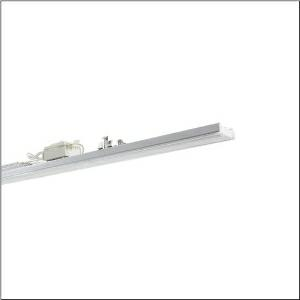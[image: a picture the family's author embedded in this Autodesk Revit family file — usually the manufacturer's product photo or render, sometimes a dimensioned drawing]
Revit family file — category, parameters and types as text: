
# Revit family: licross_r__21_recessed_ho_52tl12cn495m_a1ad
name_source: partatom
category: Lighting Fixtures
units: mm (PartAtom-declared; Revit-internal decimal feet)

## family parameters
Cut with Voids When Loaded = No
Host = Face
Light Source = No
Part Type = Normal
Room Calculation Point = No
Round Connector Dimension = Use Diameter
Shared = No

## types (1)
- --- (1 x LED, 10000 lm, 53 W, 4000K)
    Apparent Load = 53 VA
    CIE Flux Codes = 69 91 98 100 100
    Color Rendering = 80
    Color Temperature = 4000K
    Default Elevation = 1800 mm
    Description = Licross® 21 Recessed HO, luminaire insert, of sheet steel, galvanised, coil coated, white, length: 1.500mm, width: 66mm, height: 67mm, LED rated luminous flux: 9.990lm, light colour: 840, control gear: ON/OFF Multilumen, CLOi, control gear: ECG Multilumen, with plug, 3-pole, with phase selection, mains connection: 220..240V, AC, 50/60Hz, internal wiring halogen-free, primary optical cover: cover, of PMMA, light emission: direct distribution, primary light characteristic: symmetric, protection rating (complete): IP40, insulation class (complete): insulation class I (protective earthing), certification: CE, ENEC, VDE, UKCA, protection symbol: D if used in an environment without relevant dust loads with corresponding accessories, impact resistance: IK06, permissible ambient temperature for indoor applications: -35..+35°C, corresponds to IFS (International Featured Standards) requirements for safety and quality in the food industry, reducing of maximum allowable ambient temperature of 5°C with ceiling mounting, LABS conformity tested according to VDMA 24364:2018-05, packaging unit: 1 piece
    Height = 58 mm
    Lamp = 1 x LED
    Lamp Light Flux = 10000 lm
    Lamp Power = 53 W
    Lamp count = 1
    Length = 1500 mm
    Luminous efficacy = 189 lm/W
    Manufacturer = Siteco
    ModVariant = No
    Model = 52TL12CN495M
    Mounting Place = Ceiling
    Mounting Type = Pendant
    Number of Poles = 1
    OnlyDefault = Yes
    Power Factor = 1
    Product Name = Licross® 21 Recessed HO
    Product group = luminaire insert | ceiling pendant
    ProductGroupID = 902
    Protection Class = Protection class I
    Protection Degree = IP 40
    RLX_Detail_Level = 1
    RLX_Emergency_Light_Flux = 0 lm
    RLX_Emergency_Type = 0
    RLX_Emergency_Type_DB = No
    RlxData = <blob elided: 22349 chars, md5=ef7d01a0>
    Socket = socket
    Standby Power = 0 W
    System Light Flux = 10000 lm
    System Power = 53 W
    Type Comments = factory setting: luminous flux: 100 % | (A | C | E) | 125 mA
    Type Image = l_1296930.jpg
    URL = http://relux.com
    VarID = @adj_131291
    Voltage = 0 V
    Weight = 0.00 kg
    Width = 66 mm

## geometry (parser evidence)
native form markers: Blend x4, Sweep x11
no freeform markers — native parametric forms only
